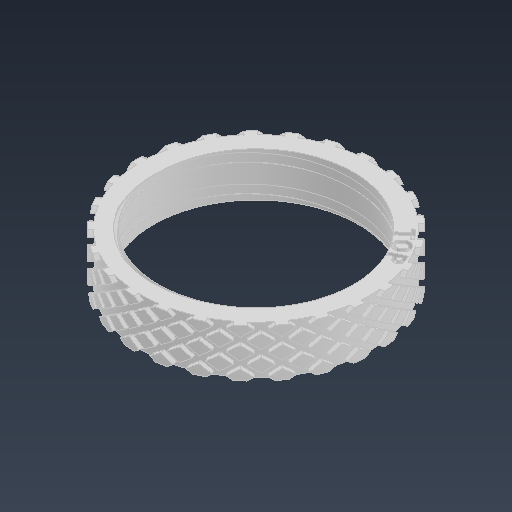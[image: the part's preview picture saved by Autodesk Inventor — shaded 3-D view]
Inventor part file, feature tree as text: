
AUTODESK INVENTOR PART (.ipt)
format: ipt  version: 2021.3 (Build 253353000, 353)  size: 1,633,792 bytes
history: native  units: mm
features: helix x6, sketch x5, extrude x2, pattern_circular x2, draft x1, projected_geometry x1
ambient origin geometry x8: Origin, YZ Plane, XZ Plane, XY Plane, X Axis, Y Axis, Z Axis, Center Point
bodies: Solid1 (feature_tree)
feature tree (17):
  extrude  "Extrusion1"  Depth=6.52mm TaperAngle=0.0deg
  draft  "FaceDraft1"
  sketch  "Sketch2"  dims[d7=4.0mm d8=9.0mm d9=10.0mm d10=1.047198mm d11=90.0deg d12=90.0deg d13=0.0mm d14=0.0mm d15=4.0mm d16=3.0mm d17=10.0mm d18=-1.047198mm d19=90.0deg d20=90.0deg d21=0.0mm d22=0.0mm d23=3.0mm]
  sketch  "Sketch4"  dims[d52=70.0mm d53=9.0mm d54=10.0mm d55=0.0mm d56=90.0deg d57=90.0deg d58=0.0mm d59=0.0mm d60=70.0mm d61=9.0mm d62=10.0mm d63=0.0mm d64=90.0deg d65=90.0deg d66=0.0mm d67=0.0mm d68=250.0mm d69=360.0deg]
  helix  "Coil1"  [1 undecoded]
  helix  "Coil2"  [1 undecoded]
  sketch  "Sketch7"  dims[d71=70.0mm d72=9.0mm d73=10.0mm d74=0.0mm d75=90.0deg d76=90.0deg d77=0.0mm d78=0.0mm d79=70.0mm d80=9.0mm d81=10.0mm d82=0.0mm d83=90.0deg d84=90.0deg d85=0.0mm d86=0.0mm d87=250.0mm d88=360.0deg d91=0.8mm d92=0.0mm]
  helix  "Coil6"  [1 undecoded]
  helix  "Coil7"  [1 undecoded]
  pattern_circular  "Circular Pattern1"  [2 undecoded]
  helix  "Coil8"  [1 undecoded]
  helix  "Coil9"  [1 undecoded]
  pattern_circular  "Circular Pattern2"  [2 undecoded]
  extrude  "Extrusion2"  [1 undecoded]
  sketch  "Sketch1"  dims[d0=26.5mm d2=6.52mm d3=0.0mm d4=1.047198mm]
  sketch  "Sketch9"
  projected_geometry  "Projected Loop1"
note: 11 required parameter values undecoded (feature->parameter linkage not recoverable at this tier; creation-order binding heuristic only, values carry confidence <= 0.55)
